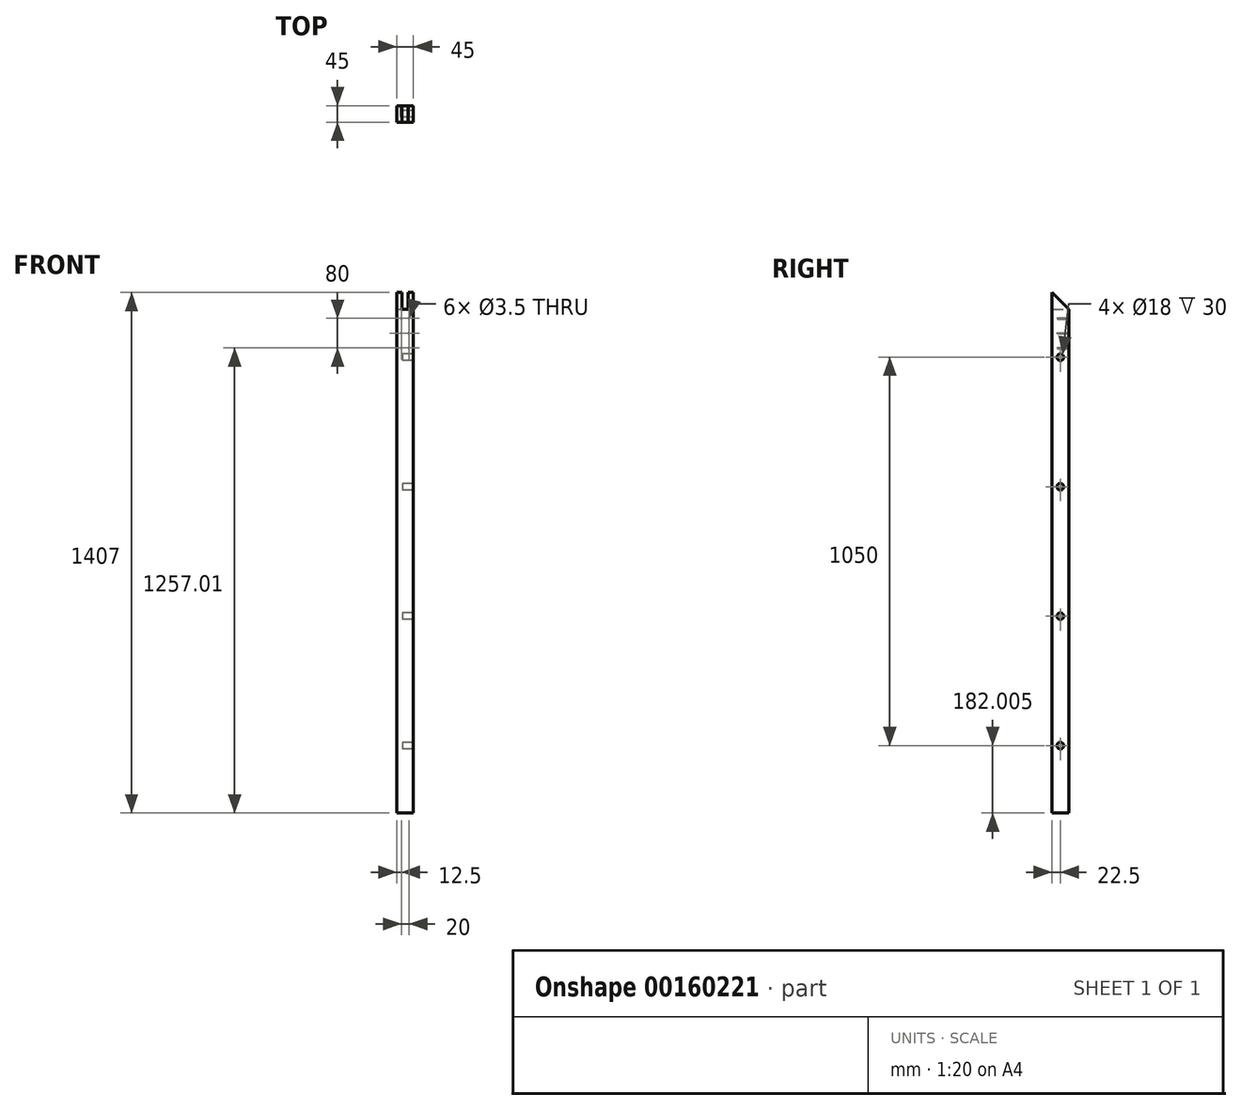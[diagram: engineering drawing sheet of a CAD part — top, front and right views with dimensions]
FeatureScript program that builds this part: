
annotation { "Feature Type Name" : "Feature", "Feature Type Description" : "" }
export const myFeature = defineFeature(function(context is Context, id is Id, definition is map)
    precondition{}
    {
        {
            var Q0;
            Q0=qCreatedBy(makeId("Front.planeOp"),FACE);
            var sketch = newSketch(context, id + "F0", { "sketchPlane" : qUnion([Q0])});
            skLineSegment(sketch, "E0.bottom", {"start": v(-22.5, 213.33) * mm, "end": v(22.5, 213.33) * mm});
            skLineSegment(sketch, "E0.top", {"start": v(-22.5, -1193.67) * mm, "end": v(22.5, -1193.67) * mm});
            skLineSegment(sketch, "E0.left", {"start": v(-22.5, 213.33) * mm, "end": v(-22.5, -1193.67) * mm});
            skLineSegment(sketch, "E0.right", {"start": v(22.5, 213.33) * mm, "end": v(22.5, -1193.67) * mm});
            skSolve(sketch);
        }
        {
            var Q0;
            Q0=makeQuery(id+"F0.imprint","IMPRINT",FACE,{"disambiguationData":[TD([[makeQuery(id+"F0.imprint","IMPRINT",EDGE,{"derivedFrom":sQuery(id+"F0.wireOp",EDGE,"E0.bottom")}),-1.0]])]});
            extrude(context, id + "F1", {"entities" : qUnion([Q0]), "endBound" : BoundingType.SYMMETRIC, "depth" : 45 * mm});
        }
        {
            var Q0;
            Q0=makeQuery(id+"F1.opExtrude","SWEPT_FACE",FACE,{"disambiguationData":[OSD([sQuery(id+"F0.wireOp",EDGE,"E0.bottom")])]});
            var sketch = newSketch(context, id + "F2", { "sketchPlane" : qUnion([Q0])});
            skLineSegment(sketch, "E1.bottom", {"start": v(8.2, -22.5) * mm, "end": v(22.5, -22.5) * mm});
            skLineSegment(sketch, "E1.top", {"start": v(8.2, 22.5) * mm, "end": v(22.5, 22.5) * mm});
            skLineSegment(sketch, "E1.left", {"start": v(8.2, -22.5) * mm, "end": v(8.2, 22.5) * mm});
            skLineSegment(sketch, "E1.right", {"start": v(22.5, -22.5) * mm, "end": v(22.5, 22.5) * mm});
            skLineSegment(sketch, "E2.bottom", {"start": v(-22.5, 22.5) * mm, "end": v(-8.2, 22.5) * mm});
            skLineSegment(sketch, "E2.top", {"start": v(-22.5, -22.5) * mm, "end": v(-8.2, -22.5) * mm});
            skLineSegment(sketch, "E2.left", {"start": v(-22.5, 22.5) * mm, "end": v(-22.5, -22.5) * mm});
            skLineSegment(sketch, "E2.right", {"start": v(-8.2, 22.5) * mm, "end": v(-8.2, -22.5) * mm});
            skSolve(sketch);
        }
        {
            var Q0;
            Q0=makeQuery(id+"F1.opExtrude","CAP_EDGE",EDGE,{"disambiguationData":[OSD([sQuery(id+"F0.wireOp",EDGE,"E0.bottom")])],"isStart":true});
            chamfer(context, id + "F3", {"entities" : qUnion([Q0]), "chamferType" : ChamferType.OFFSET_ANGLE, "width" : 45 * mm, "oppositeDirection" : false, "angle" : 45 * degree, "tangentPropagation" : true});
        }
        {
            var Q0;
            {var subQ0=sQuery(id+"F2.wireOp",EDGE,"E1.left");Q0=makeQuery(id+"F2.imprint","IMPRINT",FACE,{"disambiguationData":[TD([[makeQuery(id+"F2.imprint","IMPRINT",EDGE,{"derivedFrom":subQ0}),1.0]])]});}
            extrude(context, id + "F4", {"entities" : qUnion([Q0]), "operationType" : NewBodyOperationType.REMOVE, "oppositeDirection" : true, "depth" : 45 * mm});
        }
        {
            var Q0;
            Q0=makeQuery(id+"F1.opExtrude","SWEPT_FACE",FACE,{"disambiguationData":[OSD([sQuery(id+"F0.wireOp",EDGE,"E0.left")])]});
            var sketch = newSketch(context, id + "F5", { "sketchPlane" : qUnion([Q0])});
            skCircle(sketch, "E3", {"center": v(0, 38.33) * mm, "radius": 9 * mm});
            skCircle(sketch, "E4", {"center": v(0, -311.67) * mm, "radius": 9 * mm});
            skCircle(sketch, "E5", {"center": v(0, -661.67) * mm, "radius": 9 * mm});
            skCircle(sketch, "E6", {"center": v(0, -1011.67) * mm, "radius": 9 * mm});
            skSolve(sketch);
        }
        {
            var Q0;
            Q0=makeQuery(id+"F5.imprint","IMPRINT",FACE,{"disambiguationData":[TD([[makeQuery(id+"F5.imprint","IMPRINT",EDGE,{"derivedFrom":sQuery(id+"F5.wireOp",EDGE,"E3")}),1.0]])]});
            var Q1;
            Q1=makeQuery(id+"F5.imprint","IMPRINT",FACE,{"disambiguationData":[TD([[makeQuery(id+"F5.imprint","IMPRINT",EDGE,{"derivedFrom":sQuery(id+"F5.wireOp",EDGE,"E4")}),1.0]])]});
            var Q2;
            Q2=makeQuery(id+"F5.imprint","IMPRINT",FACE,{"disambiguationData":[TD([[makeQuery(id+"F5.imprint","IMPRINT",EDGE,{"derivedFrom":sQuery(id+"F5.wireOp",EDGE,"E5")}),1.0]])]});
            var Q3;
            Q3=makeQuery(id+"F5.imprint","IMPRINT",FACE,{"disambiguationData":[TD([[makeQuery(id+"F5.imprint","IMPRINT",EDGE,{"derivedFrom":sQuery(id+"F5.wireOp",EDGE,"E6")}),1.0]])]});
            extrude(context, id + "F6", {"entities" : qUnion([Q0, Q1, Q2, Q3]), "operationType" : NewBodyOperationType.REMOVE, "endBound" : BoundingType.THROUGH_ALL, "oppositeDirection" : true, "depth" : 20 * mm});
        }
        {
            var Q0;
            Q0=makeQuery(id+"F5.imprint","IMPRINT",FACE,{"disambiguationData":[TD([[makeQuery(id+"F5.imprint","IMPRINT",EDGE,{"derivedFrom":sQuery(id+"F5.wireOp",EDGE,"E6")}),1.0]])]});
            var Q1;
            Q1=makeQuery(id+"F5.imprint","IMPRINT",FACE,{"disambiguationData":[TD([[makeQuery(id+"F5.imprint","IMPRINT",EDGE,{"derivedFrom":sQuery(id+"F5.wireOp",EDGE,"E5")}),1.0]])]});
            var Q2;
            Q2=makeQuery(id+"F5.imprint","IMPRINT",FACE,{"disambiguationData":[TD([[makeQuery(id+"F5.imprint","IMPRINT",EDGE,{"derivedFrom":sQuery(id+"F5.wireOp",EDGE,"E4")}),1.0]])]});
            var Q3;
            Q3=makeQuery(id+"F5.imprint","IMPRINT",FACE,{"disambiguationData":[TD([[makeQuery(id+"F5.imprint","IMPRINT",EDGE,{"derivedFrom":sQuery(id+"F5.wireOp",EDGE,"E3")}),1.0]])]});
            extrude(context, id + "F7", {"entities" : qUnion([Q0, Q1, Q2, Q3]), "operationType" : NewBodyOperationType.ADD, "oppositeDirection" : true, "depth" : 15 * mm});
        }
        {
            var Q0;
            Q0=makeQuery(id+"F1.opExtrude","CAP_FACE",FACE,{"disambiguationData":[OSD([sQuery(id+"F0.wireOp",EDGE,"E0.bottom"),sQuery(id+"F0.wireOp",EDGE,"E0.top"),sQuery(id+"F0.wireOp",EDGE,"E0.left"),sQuery(id+"F0.wireOp",EDGE,"E0.right")])],"isStart":true});
            var sketch = newSketch(context, id + "F8", { "sketchPlane" : qUnion([Q0])});
            skPoint(sketch, "E7", {"position": v(22.5, 168.33) * mm});
            skPoint(sketch, "E8", {"position": v(22.5, -1193.67) * mm});
            skPoint(sketch, "E9", {"position": v(10, 143.33) * mm});
            skPoint(sketch, "E10", {"position": v(10, 103.33) * mm});
            skPoint(sketch, "E11", {"position": v(10, 63.33) * mm});
            skPoint(sketch, "E12", {"position": v(-10, 143.33) * mm});
            skPoint(sketch, "E13", {"position": v(-10, 103.33) * mm});
            skPoint(sketch, "E14", {"position": v(-10, 63.33) * mm});
            skSolve(sketch);
        }
        {
            var Q0;
            Q0=sQuery(id+"F8.wireOp",VERTEX,"E9");
            var Q1;
            Q1=sQuery(id+"F8.wireOp",VERTEX,"E10");
            var Q2;
            Q2=sQuery(id+"F8.wireOp",VERTEX,"E11");
            var Q3;
            Q3=sQuery(id+"F8.wireOp",VERTEX,"E14");
            var Q4;
            Q4=sQuery(id+"F8.wireOp",VERTEX,"E13");
            var Q5;
            Q5=sQuery(id+"F8.wireOp",VERTEX,"E12");
            var Q6;
            Q6=makeQuery(id+"F1.opExtrude","SWEPT_BODY",BODY,{"disambiguationData":[OSD([sQuery(id+"F0.wireOp",EDGE,"E0.bottom"),sQuery(id+"F0.wireOp",EDGE,"E0.top"),sQuery(id+"F0.wireOp",EDGE,"E0.left"),sQuery(id+"F0.wireOp",EDGE,"E0.right")])]});
            hole(context, id + "F9", {"style" : HoleStyle.SIMPLE, "endStyle" : HoleEndStyle.BLIND, "holeDiameter" : 3.5 * mm, "holeDepth" : 30 * mm, "startFromSketch" : true, "locations" : qUnion([Q0, Q1, Q2, Q3, Q4, Q5]), "scope" : qUnion([Q6])});
        }
    });
